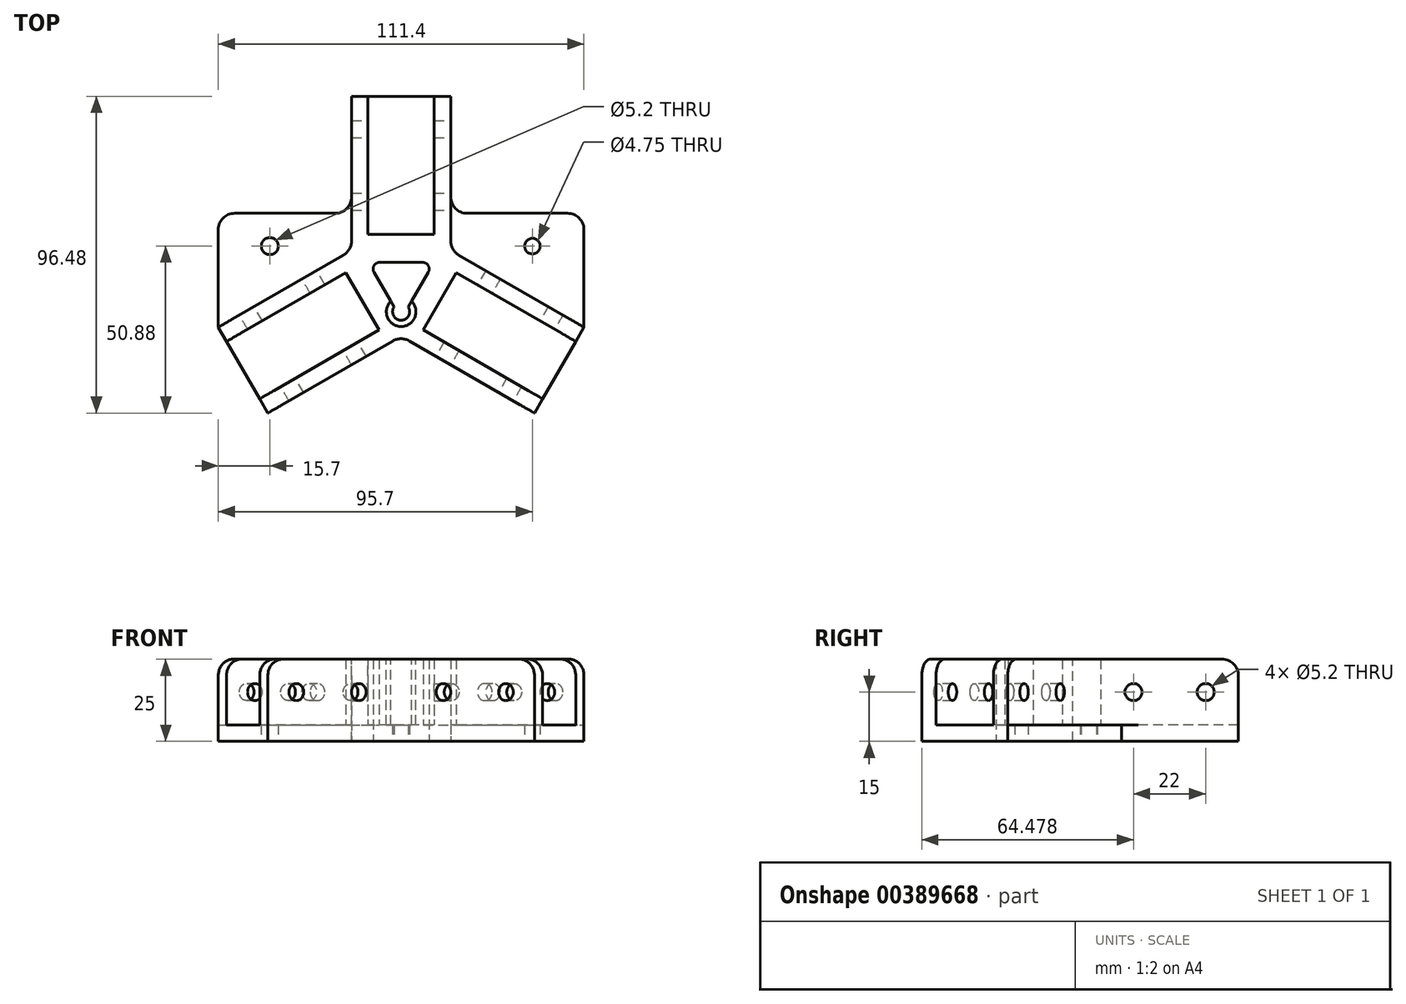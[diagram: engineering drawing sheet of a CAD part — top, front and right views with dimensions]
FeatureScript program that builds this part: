
annotation { "Feature Type Name" : "Feature", "Feature Type Description" : "" }
export const myFeature = defineFeature(function(context is Context, id is Id, definition is map)
    precondition{}
    {
        {
            var Q0;
            Q0=qCreatedBy(makeId("Top.planeOp"),FACE);
            var sketch = newSketch(context, id + "F0", { "sketchPlane" : qUnion([Q0])});
            skLineSegment(sketch, "E0", {"start": v(0, 0) * mm, "end": v(164.54, -95) * mm, "construction": true});
            skLineSegment(sketch, "E1", {"start": v(0, 0) * mm, "end": v(0, 45.49) * mm, "construction": true});
            skLineSegment(sketch, "E2", {"start": v(6.73, -15.55) * mm, "end": v(43.1, -36.55) * mm});
            skLineSegment(sketch, "E3", {"start": v(40.6, -40.88) * mm, "end": v(43.1, -36.55) * mm});
            skLineSegment(sketch, "E4", {"start": v(53.2, -19.05) * mm, "end": v(16.83, 1.95) * mm});
            skLineSegment(sketch, "E5", {"start": v(-0.2, -17.32) * mm, "end": v(40.6, -40.88) * mm});
            skLineSegment(sketch, "E6", {"start": v(55.7, -14.72) * mm, "end": v(14.9, 8.83) * mm});
            skLineSegment(sketch, "E7.trimOffspring", {"start": v(53.2, -19.05) * mm, "end": v(55.7, -14.72) * mm});
            skPoint(sketch, "E8.startSnap0", {"position": v(7.5, -4.33) * mm});
            skPoint(sketch, "E9.orphan", {"position": v(0, -11.66) * mm});
            skLineSegment(sketch, "E10", {"start": v(6.73, -15.55) * mm, "end": v(16.83, 1.95) * mm});
            skLineSegment(sketch, "E11", {"start": v(14.9, 8.83) * mm, "end": v(0, 0) * mm});
            skLineSegment(sketch, "E12", {"start": v(0, 0) * mm, "end": v(-0.2, -17.32) * mm});
            skPoint(sketch, "E13.endSnap0", {"position": v(11.78, -6.8) * mm});
            skLineSegment(sketch, "E14", {"start": v(16.86, 1.81) * mm, "end": v(6.86, -15.5) * mm, "construction": true});
            skLineSegment(sketch, "E15", {"start": v(6.86, -15.5) * mm, "end": v(171.4, -110.5) * mm, "construction": true});
            skLineSegment(sketch, "E16", {"start": v(181.4, -93.19) * mm, "end": v(16.86, 1.81) * mm, "construction": true});
            skLineSegment(sketch, "E17.bottom", {"start": v(-152.4, 152.4) * mm, "end": v(152.4, 152.4) * mm, "construction": true});
            skLineSegment(sketch, "E17.top", {"start": v(-152.4, -152.4) * mm, "end": v(152.4, -152.4) * mm, "construction": true});
            skLineSegment(sketch, "E17.left", {"start": v(-152.4, 152.4) * mm, "end": v(-152.4, -152.4) * mm, "construction": true});
            skLineSegment(sketch, "E17.right", {"start": v(152.4, 152.4) * mm, "end": v(152.4, -152.4) * mm, "construction": true});
            skLineSegment(sketch, "E18.bottom", {"start": v(-250, 230) * mm, "end": v(250, 230) * mm, "construction": true});
            skLineSegment(sketch, "E18.top", {"start": v(-250, -230) * mm, "end": v(1430.65, -230) * mm, "construction": true});
            skLineSegment(sketch, "E18.left", {"start": v(-250, 230) * mm, "end": v(-250, -230) * mm, "construction": true});
            skLineSegment(sketch, "E19.top", {"start": v(-250, 250) * mm, "end": v(250, 250) * mm, "construction": true});
            skLineSegment(sketch, "E19.left", {"start": v(-250, 230) * mm, "end": v(-250, 250) * mm, "construction": true});
            skLineSegment(sketch, "E19.right", {"start": v(250, 230) * mm, "end": v(250, 250) * mm, "construction": true});
            skLineSegment(sketch, "E20.bottom", {"start": v(-250, 250) * mm, "end": v(-270, 250) * mm, "construction": true});
            skLineSegment(sketch, "E20.top", {"start": v(-250, -250) * mm, "end": v(-270, -250) * mm, "construction": true});
            skLineSegment(sketch, "E20.left", {"start": v(-250, 250) * mm, "end": v(-250, -250) * mm, "construction": true});
            skLineSegment(sketch, "E20.right", {"start": v(-270, 250) * mm, "end": v(-270, -250) * mm, "construction": true});
            skLineSegment(sketch, "E21.bottom", {"start": v(250, 250) * mm, "end": v(270, 250) * mm, "construction": true});
            skLineSegment(sketch, "E21.top", {"start": v(250, -250) * mm, "end": v(270, -250) * mm, "construction": true});
            skLineSegment(sketch, "E21.left", {"start": v(250, 250) * mm, "end": v(250, -117.97) * mm, "construction": true});
            skLineSegment(sketch, "E21.right", {"start": v(270, 250) * mm, "end": v(270, -250) * mm, "construction": true});
            skLineSegment(sketch, "E22.bottom", {"start": v(-250, -250) * mm, "end": v(1430.65, -250) * mm, "construction": true});
            skLineSegment(sketch, "E22.left", {"start": v(-250, -250) * mm, "end": v(-250, -230) * mm, "construction": true});
            skLineSegment(sketch, "E22.right", {"start": v(1430.65, -250) * mm, "end": v(1430.65, -230) * mm, "construction": true});
            skLineSegment(sketch, "E23", {"start": v(260, -238.46) * mm, "end": v(260, 217.54) * mm, "construction": true});
            skLineSegment(sketch, "E24.trimOffspring", {"start": v(250, -117.97) * mm, "end": v(250, -250) * mm, "construction": true});
            skPoint(sketch, "E25", {"position": v(152.4, -87.99) * mm});
            skLineSegment(sketch, "E26", {"start": v(171.4, -110.5) * mm, "end": v(181.4, -93.19) * mm, "construction": true});
            skSolve(sketch);
        }
        {
            var Q0;
            Q0=qSketchRegion(id+"F0",true);
            extrude(context, id + "F1", {"entities" : qUnion([Q0]), "depth" : 20 * mm});
        }
        {
            var Q0;
            Q0=makeQuery(id+"F8AnNkQhTy7cih4_3.boolean.opBoolean","MERGE",FACE,{"derivedFrom":[makeQuery(id+"F1.opExtrude","SWEPT_FACE",FACE,{"disambiguationData":[OSD([sQuery(id+"F0.wireOp",EDGE,"E5")])]}),makeQuery(id+"F8AnNkQhTy7cih4_3.opExtrude","SWEPT_FACE",FACE,{"disambiguationData":[OSD([sQuery(id+"FXKs39bWKYu9lIt_3.wireOp",EDGE,"d46a372c-ea87-446f-ae03-e79ca4958cda.0")])]})]});
            var sketch = newSketch(context, id + "F2", { "sketchPlane" : qUnion([Q0])});
            skCircle(sketch, "E27", {"center": v(45.6, 10) * mm, "radius": 2.6 * mm});
            skCircle(sketch, "E28", {"center": v(23.6, 10) * mm, "radius": 2.6 * mm});
            skSolve(sketch);
        }
        {
            var Q0;
            Q0=qSketchRegion(id+"F2",true);
            extrude(context, id + "F3", {"entities" : qUnion([Q0]), "operationType" : NewBodyOperationType.REMOVE, "endBound" : BoundingType.THROUGH_ALL, "oppositeDirection" : true, "depth" : 25 * mm});
        }
        {
            var Q0;
            Q0=makeQuery(id+"F1.opExtrude","SWEPT_BODY",BODY,{"disambiguationData":[OSD([sQuery(id+"F0.wireOp",EDGE,"E2"),sQuery(id+"F0.wireOp",EDGE,"E3"),sQuery(id+"F0.wireOp",EDGE,"E4"),sQuery(id+"F0.wireOp",EDGE,"E5"),sQuery(id+"F0.wireOp",EDGE,"E6"),sQuery(id+"F0.wireOp",EDGE,"E7.trimOffspring"),sQuery(id+"F0.wireOp",EDGE,"E10"),sQuery(id+"F0.wireOp",EDGE,"E11"),sQuery(id+"F0.wireOp",EDGE,"E12")])]});
            var Q1;
            Q1=makeQuery(id+"F1.opExtrude","SWEPT_EDGE",EDGE,{"disambiguationData":[OSD([sQuery(id+"F0.wireOp",EDGE,"E11"),sQuery(id+"F0.wireOp",EDGE,"E12")])]});
            circularPattern(context, id + "F4", {"operationType" : NewBodyOperationType.ADD, "entities" : qUnion([Q0]), "axis" : qUnion([Q1]), "angle" : 120 * degree, "instanceCount" : round(3)});
        }
        {
            var Q0;
            {var subQ0=makeQuery(id+"F1.opExtrude","CAP_FACE",FACE,{"disambiguationData":[OSD([sQuery(id+"F0.wireOp",EDGE,"E2"),sQuery(id+"F0.wireOp",EDGE,"E3"),sQuery(id+"F0.wireOp",EDGE,"E4"),sQuery(id+"F0.wireOp",EDGE,"E5"),sQuery(id+"F0.wireOp",EDGE,"E6"),sQuery(id+"F0.wireOp",EDGE,"E7.trimOffspring"),sQuery(id+"F0.wireOp",EDGE,"E10"),sQuery(id+"F0.wireOp",EDGE,"E11"),sQuery(id+"F0.wireOp",EDGE,"E12")])],"isStart":true});Q0=makeQuery(id+"F4.boolean.opBoolean","MERGE",FACE,{"derivedFrom":[subQ0,makeQuery(id+"F4.opPattern","COPY",FACE,{"derivedFrom":subQ0,"instanceName":"1"}),makeQuery(id+"F4.opPattern","COPY",FACE,{"derivedFrom":subQ0,"instanceName":"2"})]});}
            var sketch = newSketch(context, id + "F5", { "sketchPlane" : qUnion([Q0])});
            skLineSegment(sketch, "E29.0", {"start": v(-40.6, 40.88) * mm, "end": v(0, 17.44) * mm});
            skLineSegment(sketch, "E30.0", {"start": v(0, 17.44) * mm, "end": v(40.6, 40.88) * mm});
            skLineSegment(sketch, "E31.0", {"start": v(55.7, 14.72) * mm, "end": v(15.1, -8.72) * mm});
            skLineSegment(sketch, "E32.0", {"start": v(15.1, -8.72) * mm, "end": v(15.1, -55.6) * mm});
            skLineSegment(sketch, "E33.0", {"start": v(-15.1, -55.6) * mm, "end": v(-15.1, -8.72) * mm});
            skLineSegment(sketch, "E34.0", {"start": v(-15.1, -8.72) * mm, "end": v(-55.7, 14.72) * mm});
            skLineSegment(sketch, "E35", {"start": v(-40.6, 40.88) * mm, "end": v(-55.7, 14.72) * mm});
            skLineSegment(sketch, "E36", {"start": v(40.6, 40.88) * mm, "end": v(55.7, 14.72) * mm});
            skLineSegment(sketch, "E37", {"start": v(15.1, -55.6) * mm, "end": v(-15.1, -55.6) * mm});
            skSolve(sketch);
        }
        {
            var Q0;
            Q0=qSketchRegion(id+"F5",true);
            extrude(context, id + "F6", {"entities" : qUnion([Q0]), "operationType" : NewBodyOperationType.ADD, "depth" : 5 * mm});
        }
        {
            var Q0;
            Q0=makeQuery(id+"F6.boolean.opBoolean","MERGE",EDGE,{"derivedFrom":[makeQuery(id+"F4.boolean.opBoolean","INTERSECT",EDGE,{"derivedFrom":[makeQuery(id+"F1.opExtrude","SWEPT_FACE",FACE,{"disambiguationData":[OSD([sQuery(id+"F0.wireOp",EDGE,"E5")])]}),makeQuery(id+"F4.opPattern","COPY",FACE,{"derivedFrom":makeQuery(id+"F1.opExtrude","SWEPT_FACE",FACE,{"disambiguationData":[OSD([sQuery(id+"F0.wireOp",EDGE,"E6")])]}),"instanceName":"1"})]}),makeQuery(id+"F6.opExtrude","SWEPT_EDGE",EDGE,{"disambiguationData":[OSD([sQuery(id+"F5.wireOp",EDGE,"E29.0"),sQuery(id+"F5.wireOp",EDGE,"E30.0")])]})]});
            var Q1;
            Q1=makeQuery(id+"F6.boolean.opBoolean","MERGE",EDGE,{"derivedFrom":[makeQuery(id+"F4.boolean.opBoolean","INTERSECT",EDGE,{"derivedFrom":[makeQuery(id+"F1.opExtrude","SWEPT_FACE",FACE,{"disambiguationData":[OSD([sQuery(id+"F0.wireOp",EDGE,"E6")])]}),makeQuery(id+"F4.opPattern","COPY",FACE,{"derivedFrom":makeQuery(id+"F1.opExtrude","SWEPT_FACE",FACE,{"disambiguationData":[OSD([sQuery(id+"F0.wireOp",EDGE,"E5")])]}),"instanceName":"2"})]}),makeQuery(id+"F6.opExtrude","SWEPT_EDGE",EDGE,{"disambiguationData":[OSD([sQuery(id+"F5.wireOp",EDGE,"E31.0"),sQuery(id+"F5.wireOp",EDGE,"E32.0")])]})]});
            var Q2;
            Q2=makeQuery(id+"F6.boolean.opBoolean","MERGE",EDGE,{"derivedFrom":[makeQuery(id+"F4.boolean.opBoolean","INTERSECT",EDGE,{"derivedFrom":[makeQuery(id+"F4.opPattern","COPY",FACE,{"derivedFrom":makeQuery(id+"F1.opExtrude","SWEPT_FACE",FACE,{"disambiguationData":[OSD([sQuery(id+"F0.wireOp",EDGE,"E5")])]}),"instanceName":"1"}),makeQuery(id+"F4.opPattern","COPY",FACE,{"derivedFrom":makeQuery(id+"F1.opExtrude","SWEPT_FACE",FACE,{"disambiguationData":[OSD([sQuery(id+"F0.wireOp",EDGE,"E6")])]}),"instanceName":"2"})]}),makeQuery(id+"F6.opExtrude","SWEPT_EDGE",EDGE,{"disambiguationData":[OSD([sQuery(id+"F5.wireOp",EDGE,"E33.0"),sQuery(id+"F5.wireOp",EDGE,"E34.0")])]})]});
            fillet(context, id + "F7", {"entities" : qUnion([Q0, Q1, Q2]), "radius" : 5 * mm, "tangentPropagation" : true, "allowEdgeOverflow" : false});
        }
        {
            var Q0;
            {var subQ0=makeQuery(id+"F1.opExtrude","CAP_FACE",FACE,{"disambiguationData":[OSD([sQuery(id+"F0.wireOp",EDGE,"E2"),sQuery(id+"F0.wireOp",EDGE,"E3"),sQuery(id+"F0.wireOp",EDGE,"E4"),sQuery(id+"F0.wireOp",EDGE,"E5"),sQuery(id+"F0.wireOp",EDGE,"E6"),sQuery(id+"F0.wireOp",EDGE,"E7.trimOffspring"),sQuery(id+"F0.wireOp",EDGE,"E10"),sQuery(id+"F0.wireOp",EDGE,"E11"),sQuery(id+"F0.wireOp",EDGE,"E12")])],"isStart":false});Q0=makeQuery(id+"F4.boolean.opBoolean","MERGE",FACE,{"derivedFrom":[subQ0,makeQuery(id+"F4.opPattern","COPY",FACE,{"derivedFrom":subQ0,"instanceName":"1"}),makeQuery(id+"F4.opPattern","COPY",FACE,{"derivedFrom":subQ0,"instanceName":"2"})]});}
            var sketch = newSketch(context, id + "F8", { "sketchPlane" : qUnion([Q0])});
            skLineSegment(sketch, "E38", {"start": v(-10, 5.06) * mm, "end": v(0, -12.26) * mm});
            skLineSegment(sketch, "E39", {"start": v(0, -12.26) * mm, "end": v(10, 5.06) * mm});
            skLineSegment(sketch, "E40", {"start": v(10, 5.06) * mm, "end": v(-10, 5.06) * mm});
            skSolve(sketch);
        }
        {
            var Q0;
            Q0=makeQuery(id+"F6.opExtrude","CAP_FACE",FACE,{"disambiguationData":[OSD([sQuery(id+"F5.wireOp",EDGE,"E29.0"),sQuery(id+"F5.wireOp",EDGE,"E30.0"),sQuery(id+"F5.wireOp",EDGE,"E31.0"),sQuery(id+"F5.wireOp",EDGE,"E32.0"),sQuery(id+"F5.wireOp",EDGE,"E33.0"),sQuery(id+"F5.wireOp",EDGE,"E34.0"),sQuery(id+"F5.wireOp",EDGE,"E35"),sQuery(id+"F5.wireOp",EDGE,"E36"),sQuery(id+"F5.wireOp",EDGE,"E37")])],"isStart":false});
            var sketch = newSketch(context, id + "F9", { "sketchPlane" : qUnion([Q0])});
            skLineSegment(sketch, "E41.top", {"start": v(-55.7, -20) * mm, "end": v(55.7, -20) * mm});
            skLineSegment(sketch, "E41.left", {"start": v(-55.7, 14.72) * mm, "end": v(-55.7, -20) * mm});
            skLineSegment(sketch, "E41.right", {"start": v(55.7, 14.72) * mm, "end": v(55.7, -20) * mm});
            skLineSegment(sketch, "E42", {"start": v(-52.65, 20) * mm, "end": v(-4.44, 20) * mm});
            skLineSegment(sketch, "E43", {"start": v(52.65, 20) * mm, "end": v(55.7, 14.72) * mm});
            skPoint(sketch, "E44.start.orphan", {"position": v(-52.65, 20) * mm});
            skLineSegment(sketch, "E45", {"start": v(-52.65, 20) * mm, "end": v(-55.7, 14.72) * mm});
            skPoint(sketch, "E46.orphan", {"position": v(-55.7, 20) * mm});
            skArc(sketch, "E47.0", {"start": v(2.5, 18.88) * mm, "mid": v(0, 18.2) * mm, "end": v(-2.5, 18.88) * mm});
            skLineSegment(sketch, "E47.1", {"start": v(2.5, 18.88) * mm, "end": v(4.44, 20) * mm});
            skLineSegment(sketch, "E47.2", {"start": v(-4.44, 20) * mm, "end": v(-2.5, 18.88) * mm});
            skPoint(sketch, "E48.orphan", {"position": v(-40.6, 40.88) * mm});
            skPoint(sketch, "E49.orphan", {"position": v(40.6, 40.88) * mm});
            skLineSegment(sketch, "E50.trimOffspring", {"start": v(4.44, 20) * mm, "end": v(52.65, 20) * mm});
            skSolve(sketch);
        }
        {
            var Q0;
            Q0=qSketchRegion(id+"F9",true);
            extrude(context, id + "F10", {"entities" : qUnion([Q0]), "operationType" : NewBodyOperationType.ADD, "oppositeDirection" : true, "depth" : 5 * mm});
        }
        {
            var Q0;
            Q0=qSketchRegion(id+"F8",true);
            extrude(context, id + "F11", {"entities" : qUnion([Q0]), "operationType" : NewBodyOperationType.REMOVE, "endBound" : BoundingType.THROUGH_ALL, "oppositeDirection" : true, "depth" : 25 * mm});
        }
        {
            var Q0;
            Q0=makeQuery(id+"F11.boolean.opBoolean","COPY",EDGE,{"derivedFrom":makeQuery(id+"F11.opExtrude","SWEPT_EDGE",EDGE,{"disambiguationData":[OSD([sQuery(id+"F8.wireOp",EDGE,"E39"),sQuery(id+"F8.wireOp",EDGE,"E40")])]})});
            var Q1;
            Q1=makeQuery(id+"F11.boolean.opBoolean","COPY",EDGE,{"derivedFrom":makeQuery(id+"F11.opExtrude","SWEPT_EDGE",EDGE,{"disambiguationData":[OSD([sQuery(id+"F8.wireOp",EDGE,"E38"),sQuery(id+"F8.wireOp",EDGE,"E40")])]})});
            var Q2;
            Q2=makeQuery(id+"F11.boolean.opBoolean","COPY",EDGE,{"derivedFrom":makeQuery(id+"F11.opExtrude","SWEPT_EDGE",EDGE,{"disambiguationData":[OSD([sQuery(id+"F8.wireOp",EDGE,"E38"),sQuery(id+"F8.wireOp",EDGE,"E39")])]})});
            fillet(context, id + "F12", {"entities" : qUnion([Q0, Q1, Q2]), "radius" : 2 * mm, "tangentPropagation" : true, "allowEdgeOverflow" : false});
        }
        {
            var Q0;
            Q0=makeQuery(id+"F10.boolean.opBoolean","MERGE",FACE,{"derivedFrom":[makeQuery(id+"F6.opExtrude","CAP_FACE",FACE,{"disambiguationData":[OSD([sQuery(id+"F5.wireOp",EDGE,"E29.0"),sQuery(id+"F5.wireOp",EDGE,"E30.0"),sQuery(id+"F5.wireOp",EDGE,"E31.0"),sQuery(id+"F5.wireOp",EDGE,"E32.0"),sQuery(id+"F5.wireOp",EDGE,"E33.0"),sQuery(id+"F5.wireOp",EDGE,"E34.0"),sQuery(id+"F5.wireOp",EDGE,"E35"),sQuery(id+"F5.wireOp",EDGE,"E36"),sQuery(id+"F5.wireOp",EDGE,"E37")])],"isStart":false}),makeQuery(id+"F10.opExtrude","CAP_FACE",FACE,{"disambiguationData":[OSD([sQuery(id+"F9.wireOp",EDGE,"E41.bottom"),sQuery(id+"F9.wireOp",EDGE,"E41.top"),sQuery(id+"F9.wireOp",EDGE,"E41.left"),sQuery(id+"F9.wireOp",EDGE,"E41.right")])],"isStart":true})]});
            var sketch = newSketch(context, id + "F13", { "sketchPlane" : qUnion([Q0])});
            skCircle(sketch, "E51", {"center": v(-40, -10) * mm, "radius": 2.6 * mm});
            skCircle(sketch, "E52", {"center": v(40, -10) * mm, "radius": 2.37 * mm});
            skCircle(sketch, "E53", {"center": v(0, 10) * mm, "radius": 2.6 * mm});
            skSolve(sketch);
        }
        {
            var Q0;
            Q0=qSketchRegion(id+"F13",true);
            extrude(context, id + "F14", {"entities" : qUnion([Q0]), "operationType" : NewBodyOperationType.REMOVE, "endBound" : BoundingType.THROUGH_ALL, "oppositeDirection" : true, "depth" : 25 * mm});
        }
        {
            var Q0;
            Q0=makeQuery(id+"F10.boolean.opBoolean","INTERSECT",EDGE,{"derivedFrom":[makeQuery(id+"F6.boolean.opBoolean","MERGE",FACE,{"derivedFrom":[makeQuery(id+"F4.opPattern","COPY",FACE,{"derivedFrom":makeQuery(id+"F1.opExtrude","SWEPT_FACE",FACE,{"disambiguationData":[OSD([sQuery(id+"F0.wireOp",EDGE,"E6")])]}),"instanceName":"2"}),makeQuery(id+"F6.opExtrude","SWEPT_FACE",FACE,{"disambiguationData":[OSD([sQuery(id+"F5.wireOp",EDGE,"E33.0")])]})]}),makeQuery(id+"F10.opExtrude","SWEPT_FACE",FACE,{"disambiguationData":[OSD([sQuery(id+"F9.wireOp",EDGE,"E41.top")])]})]});
            var Q1;
            Q1=makeQuery(id+"F10.boolean.opBoolean","INTERSECT",EDGE,{"derivedFrom":[makeQuery(id+"F6.boolean.opBoolean","MERGE",FACE,{"derivedFrom":[makeQuery(id+"F4.opPattern","COPY",FACE,{"derivedFrom":makeQuery(id+"F1.opExtrude","SWEPT_FACE",FACE,{"disambiguationData":[OSD([sQuery(id+"F0.wireOp",EDGE,"E5")])]}),"instanceName":"2"}),makeQuery(id+"F6.opExtrude","SWEPT_FACE",FACE,{"disambiguationData":[OSD([sQuery(id+"F5.wireOp",EDGE,"E32.0")])]})]}),makeQuery(id+"F10.opExtrude","SWEPT_FACE",FACE,{"disambiguationData":[OSD([sQuery(id+"F9.wireOp",EDGE,"E41.top")])]})]});
            var Q2;
            Q2=makeQuery(id+"F10.opExtrude","SWEPT_EDGE",EDGE,{"disambiguationData":[OSD([sQuery(id+"F9.wireOp",EDGE,"E41.top"),sQuery(id+"F9.wireOp",EDGE,"E41.right")])]});
            var Q3;
            Q3=makeQuery(id+"F10.opExtrude","SWEPT_EDGE",EDGE,{"disambiguationData":[OSD([sQuery(id+"F9.wireOp",EDGE,"E41.top"),sQuery(id+"F9.wireOp",EDGE,"E41.left")])]});
            var Q4;
            Q4=makeQuery(id+"F4.opPattern","COPY",EDGE,{"derivedFrom":makeQuery(id+"F1.opExtrude","CAP_EDGE",EDGE,{"disambiguationData":[OSD([sQuery(id+"F0.wireOp",EDGE,"E7.trimOffspring")])],"isStart":false}),"instanceName":"2"});
            var Q5;
            Q5=makeQuery(id+"F4.opPattern","COPY",EDGE,{"derivedFrom":makeQuery(id+"F1.opExtrude","CAP_EDGE",EDGE,{"disambiguationData":[OSD([sQuery(id+"F0.wireOp",EDGE,"E3")])],"isStart":false}),"instanceName":"2"});
            var Q6;
            Q6=makeQuery(id+"F4.opPattern","COPY",EDGE,{"derivedFrom":makeQuery(id+"F1.opExtrude","CAP_EDGE",EDGE,{"disambiguationData":[OSD([sQuery(id+"F0.wireOp",EDGE,"E3")])],"isStart":false}),"instanceName":"1"});
            var Q7;
            Q7=makeQuery(id+"F4.opPattern","COPY",EDGE,{"derivedFrom":makeQuery(id+"F1.opExtrude","CAP_EDGE",EDGE,{"disambiguationData":[OSD([sQuery(id+"F0.wireOp",EDGE,"E7.trimOffspring")])],"isStart":false}),"instanceName":"1"});
            var Q8;
            Q8=makeQuery(id+"F1.opExtrude","CAP_EDGE",EDGE,{"disambiguationData":[OSD([sQuery(id+"F0.wireOp",EDGE,"E7.trimOffspring")])],"isStart":false});
            var Q9;
            Q9=makeQuery(id+"F1.opExtrude","CAP_EDGE",EDGE,{"disambiguationData":[OSD([sQuery(id+"F0.wireOp",EDGE,"E3")])],"isStart":false});
            var Q10;
            Q10=makeQuery(id+"F10.opExtrude","SWEPT_EDGE",EDGE,{"disambiguationData":[OSD([sQuery(id+"F9.wireOp",EDGE,"E41.left"),sQuery(id+"F9.wireOp",EDGE,"E42")])]});
            var Q11;
            Q11=makeQuery(id+"F10.opExtrude","SWEPT_EDGE",EDGE,{"disambiguationData":[OSD([sQuery(id+"F9.wireOp",EDGE,"E41.right"),sQuery(id+"F9.wireOp",EDGE,"E42")])]});
            fillet(context, id + "F15", {"entities" : qUnion([Q0, Q1, Q2, Q3, Q4, Q5, Q6, Q7, Q8, Q9, Q10, Q11]), "radius" : 5 * mm, "tangentPropagation" : true, "allowEdgeOverflow" : false});
        }
        {
            var Q0;
            {var subQ0=makeQuery(id+"F1.opExtrude","CAP_FACE",FACE,{"disambiguationData":[OSD([sQuery(id+"F0.wireOp",EDGE,"E2"),sQuery(id+"F0.wireOp",EDGE,"E3"),sQuery(id+"F0.wireOp",EDGE,"E4"),sQuery(id+"F0.wireOp",EDGE,"E5"),sQuery(id+"F0.wireOp",EDGE,"E6"),sQuery(id+"F0.wireOp",EDGE,"E7.trimOffspring"),sQuery(id+"F0.wireOp",EDGE,"E10"),sQuery(id+"F0.wireOp",EDGE,"E11"),sQuery(id+"F0.wireOp",EDGE,"E12")])],"isStart":false});Q0=makeQuery(id+"F4.boolean.opBoolean","MERGE",FACE,{"derivedFrom":[subQ0,makeQuery(id+"F4.opPattern","COPY",FACE,{"derivedFrom":subQ0,"instanceName":"1"}),makeQuery(id+"F4.opPattern","COPY",FACE,{"derivedFrom":subQ0,"instanceName":"2"})]});}
            var sketch = newSketch(context, id + "F16", { "sketchPlane" : qUnion([Q0])});
            skLineSegment(sketch, "E54.0", {"start": v(-2.15, -8.54) * mm, "end": v(-2.15, -8.54) * mm});
            skCircle(sketch, "E55", {"center": v(0, -10) * mm, "radius": 4.5 * mm});
            skSolve(sketch);
        }
        {
            var Q0;
            Q0=qSketchRegion(id+"F16",true);
            extrude(context, id + "F17", {"entities" : qUnion([Q0]), "operationType" : NewBodyOperationType.REMOVE, "oppositeDirection" : true, "depth" : 20 * mm});
        }
    });
